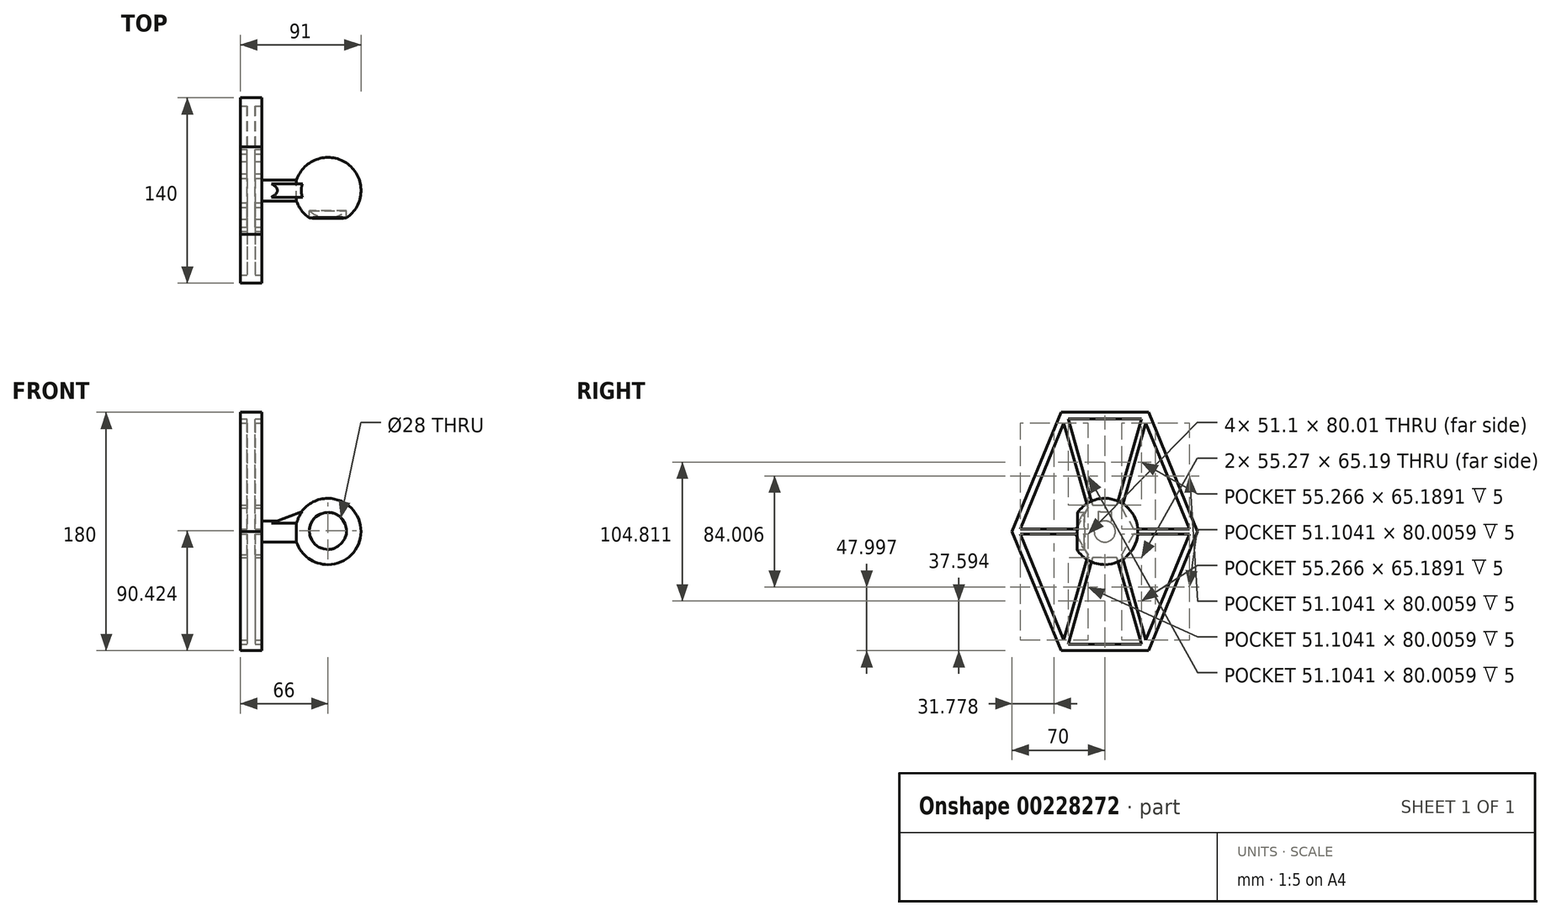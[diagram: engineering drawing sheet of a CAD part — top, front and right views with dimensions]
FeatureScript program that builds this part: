
annotation { "Feature Type Name" : "Feature", "Feature Type Description" : "" }
export const myFeature = defineFeature(function(context is Context, id is Id, definition is map)
    precondition{}
    {
        {
            var Q0;
            Q0=qCreatedBy(makeId("Front.planeOp"),FACE);
            var sketch = newSketch(context, id + "F0", { "sketchPlane" : qUnion([Q0])});
            skArc(sketch, "E0", {"start": v(0, -25) * mm, "mid": v(25, 0) * mm, "end": v(0, 25) * mm});
            skLineSegment(sketch, "E1", {"start": v(0, 25) * mm, "end": v(0, -25) * mm});
            skSolve(sketch);
        }
        {
            var Q0;
            Q0=qSketchRegion(id+"F0",true);
            var Q1;
            Q1=sQuery(id+"F0.wireOp",EDGE,"E1");
            revolve(context, id + "F1", {"entities" : qUnion([Q0]), "axis" : qUnion([Q1]), "revolveType" : RevolveType.FULL});
        }
        {
            var Q0;
            Q0=qCreatedBy(makeId("Front.planeOp"),FACE);
            var sketch = newSketch(context, id + "F2", { "sketchPlane" : qUnion([Q0])});
            skLineSegment(sketch, "E2.bottom", {"start": v(0, 0) * mm, "end": v(-55, 0) * mm});
            skLineSegment(sketch, "E2.top", {"start": v(0, 8) * mm, "end": v(-55, 8) * mm});
            skLineSegment(sketch, "E2.left", {"start": v(0, 0) * mm, "end": v(0, 8) * mm});
            skLineSegment(sketch, "E2.right", {"start": v(-55, 0) * mm, "end": v(-55, 8) * mm});
            skSolve(sketch);
        }
        {
            var Q0;
            Q0=qSketchRegion(id+"F2",true);
            var Q1;
            Q1=sQuery(id+"F2.wireOp",EDGE,"E2.bottom");
            revolve(context, id + "F3", {"operationType" : NewBodyOperationType.ADD, "entities" : qUnion([Q0]), "axis" : qUnion([Q1]), "revolveType" : RevolveType.FULL});
        }
        {
            var Q0;
            Q0=makeQuery(id+"F3.opRevolve","SWEPT_FACE",FACE,{"disambiguationData":[OSD([sQuery(id+"F2.wireOp",EDGE,"E2.right")])]});
            var sketch = newSketch(context, id + "F4", { "sketchPlane" : qUnion([Q0])});
            skLineSegment(sketch, "E3", {"start": v(0, 90) * mm, "end": v(-33.06, 90) * mm});
            skLineSegment(sketch, "E4", {"start": v(-33.06, 90) * mm, "end": v(-70, 0) * mm});
            skLineSegment(sketch, "E5", {"start": v(-70, 0) * mm, "end": v(0, 0) * mm, "construction": true});
            skLineSegment(sketch, "E6", {"start": v(0, 0) * mm, "end": v(0, 90) * mm, "construction": true});
            skLineSegment(sketch, "E7.MirrorCS", {"start": v(-33.06, -90) * mm, "end": v(-70, 0) * mm});
            skLineSegment(sketch, "E8.MirrorCS", {"start": v(0, -90) * mm, "end": v(-33.06, -90) * mm});
            skLineSegment(sketch, "E9.MirrorCS", {"start": v(0, 90) * mm, "end": v(33.06, 90) * mm});
            skLineSegment(sketch, "E10.MirrorCS", {"start": v(33.06, 90) * mm, "end": v(70, 0) * mm});
            skLineSegment(sketch, "E11.MirrorCS", {"start": v(33.06, -90) * mm, "end": v(70, 0) * mm});
            skLineSegment(sketch, "E12.MirrorCS", {"start": v(0, -90) * mm, "end": v(33.06, -90) * mm});
            skSolve(sketch);
        }
        {
            var Q0;
            Q0=qSketchRegion(id+"F4",true);
            extrude(context, id + "F5", {"entities" : qUnion([Q0]), "operationType" : NewBodyOperationType.ADD, "depth" : 6 * mm});
        }
        {
            var Q0;
            Q0=makeQuery(id+"F5.opExtrude","CAP_FACE",FACE,{"disambiguationData":[OSD([sQuery(id+"F4.wireOp",EDGE,"E3"),sQuery(id+"F4.wireOp",EDGE,"E4"),sQuery(id+"F4.wireOp",EDGE,"E7.MirrorCS"),sQuery(id+"F4.wireOp",EDGE,"E8.MirrorCS"),sQuery(id+"F4.wireOp",EDGE,"E9.MirrorCS"),sQuery(id+"F4.wireOp",EDGE,"E10.MirrorCS"),sQuery(id+"F4.wireOp",EDGE,"E11.MirrorCS"),sQuery(id+"F4.wireOp",EDGE,"E12.MirrorCS")])],"isStart":false});
            var sketch = newSketch(context, id + "F6", { "sketchPlane" : qUnion([Q0])});
            skLineSegment(sketch, "E13.0", {"start": v(-30.94, 82) * mm, "end": v(-12.67, 17.68) * mm});
            skLineSegment(sketch, "E14.0", {"start": v(-27.63, 85) * mm, "end": v(-9.12, 19.81) * mm});
            skLineSegment(sketch, "E15.0", {"start": v(-63.77, -2) * mm, "end": v(-21.72, -2) * mm});
            skLineSegment(sketch, "E16.0", {"start": v(-63.77, 2) * mm, "end": v(-21.72, 2) * mm});
            skLineSegment(sketch, "E17", {"start": v(0, 0) * mm, "end": v(0, -57.76) * mm, "construction": true});
            skLineSegment(sketch, "E18", {"start": v(0, 0) * mm, "end": v(92.77, 0) * mm, "construction": true});
            skLineSegment(sketch, "E19.MirrorCS", {"start": v(63.77, -2) * mm, "end": v(21.72, -2) * mm});
            skLineSegment(sketch, "E20.MirrorCS", {"start": v(63.77, 2) * mm, "end": v(21.72, 2) * mm});
            skLineSegment(sketch, "E21.MirrorCS", {"start": v(30.94, 82) * mm, "end": v(12.67, 17.68) * mm});
            skLineSegment(sketch, "E22.MirrorCS", {"start": v(27.63, 85) * mm, "end": v(9.12, 19.81) * mm});
            skLineSegment(sketch, "E23.MirrorCS", {"start": v(-30.94, -82) * mm, "end": v(-12.67, -17.68) * mm});
            skLineSegment(sketch, "E24.MirrorCS", {"start": v(-27.63, -85) * mm, "end": v(-9.12, -19.81) * mm});
            skLineSegment(sketch, "E25.MirrorCS", {"start": v(27.63, -85) * mm, "end": v(9.12, -19.81) * mm});
            skLineSegment(sketch, "E26.MirrorCS", {"start": v(30.94, -82) * mm, "end": v(12.67, -17.68) * mm});
            skLineSegment(sketch, "E27.0", {"start": v(-9.12, 19.81) * mm, "end": v(9.12, 19.81) * mm});
            skLineSegment(sketch, "E27.1", {"start": v(12.67, 17.68) * mm, "end": v(21.72, 2) * mm});
            skLineSegment(sketch, "E27.2", {"start": v(21.72, -2) * mm, "end": v(12.67, -17.68) * mm});
            skLineSegment(sketch, "E27.3", {"start": v(9.12, -19.81) * mm, "end": v(-9.12, -19.81) * mm});
            skLineSegment(sketch, "E27.4", {"start": v(-12.67, -17.68) * mm, "end": v(-21.72, -2) * mm});
            skLineSegment(sketch, "E27.5", {"start": v(-21.72, 2) * mm, "end": v(-12.67, 17.68) * mm});
            skPoint(sketch, "E27.0.midPoint", {"position": v(0, 19.81) * mm});
            skPoint(sketch, "E28.end.orphan", {"position": v(-10.36, 9.54) * mm});
            skPoint(sketch, "E28.start.orphan", {"position": v(-6.97, 12.24) * mm});
            skPoint(sketch, "E29.orphan", {"position": v(-11.44, 19.81) * mm});
            skPoint(sketch, "E30.end.orphan", {"position": v(6.97, 12.24) * mm});
            skPoint(sketch, "E30.start.orphan", {"position": v(10.36, 9.54) * mm});
            skPoint(sketch, "E31.orphan", {"position": v(11.44, 19.81) * mm});
            skPoint(sketch, "E32.orphan", {"position": v(14.09, 2) * mm});
            skPoint(sketch, "E33.MirrorCS.end.orphan", {"position": v(14.09, -2) * mm});
            skPoint(sketch, "E34.end.orphan", {"position": v(10.36, -9.54) * mm});
            skPoint(sketch, "E35.orphan", {"position": v(6.97, -12.24) * mm});
            skPoint(sketch, "E36.end.orphan", {"position": v(-6.97, -12.24) * mm});
            skPoint(sketch, "E36.start.orphan", {"position": v(-10.36, -9.54) * mm});
            skPoint(sketch, "E37.end.orphan", {"position": v(-14.09, -2) * mm});
            skPoint(sketch, "E37.start.orphan", {"position": v(-14.09, 2) * mm});
            skLineSegment(sketch, "E38.0", {"start": v(-33.06, 90) * mm, "end": v(-70, 0) * mm});
            skLineSegment(sketch, "E38.1", {"start": v(-33.06, -90) * mm, "end": v(33.06, -90) * mm});
            skLineSegment(sketch, "E38.2", {"start": v(33.06, -90) * mm, "end": v(70, 0) * mm});
            skLineSegment(sketch, "E38.3", {"start": v(-70, 0) * mm, "end": v(-33.06, -90) * mm});
            skLineSegment(sketch, "E38.4", {"start": v(70, 0) * mm, "end": v(33.06, 90) * mm});
            skLineSegment(sketch, "E38.5", {"start": v(33.06, 90) * mm, "end": v(-33.06, 90) * mm});
            skLineSegment(sketch, "E39.0", {"start": v(27.63, 85) * mm, "end": v(-27.63, 85) * mm});
            skLineSegment(sketch, "E39.1", {"start": v(-63.77, -2) * mm, "end": v(-30.94, -82) * mm});
            skLineSegment(sketch, "E39.2", {"start": v(-27.63, -85) * mm, "end": v(27.63, -85) * mm});
            skLineSegment(sketch, "E39.3", {"start": v(-30.94, 82) * mm, "end": v(-63.77, 2) * mm});
            skLineSegment(sketch, "E39.4", {"start": v(30.94, -82) * mm, "end": v(63.77, -2) * mm});
            skLineSegment(sketch, "E39.5", {"start": v(63.77, 2) * mm, "end": v(30.94, 82) * mm});
            skPoint(sketch, "E40.orphan", {"position": v(-31.64, 84.45) * mm});
            skPoint(sketch, "E41.orphan", {"position": v(-27.79, 85.55) * mm});
            skPoint(sketch, "E42.orphan", {"position": v(31.64, 84.45) * mm});
            skPoint(sketch, "E43.orphan", {"position": v(27.79, 85.55) * mm});
            skPoint(sketch, "E44.orphan", {"position": v(64.6, 2) * mm});
            skPoint(sketch, "E45.MirrorCS.end.orphan", {"position": v(64.6, -2) * mm});
            skPoint(sketch, "E46.orphan", {"position": v(31.64, -84.45) * mm});
            skPoint(sketch, "E47.orphan", {"position": v(27.79, -85.55) * mm});
            skPoint(sketch, "E48.orphan", {"position": v(-31.64, -84.45) * mm});
            skPoint(sketch, "E49.orphan", {"position": v(-27.79, -85.55) * mm});
            skPoint(sketch, "E50.orphan", {"position": v(-64.6, 2) * mm});
            skPoint(sketch, "E51.orphan", {"position": v(-64.6, -2) * mm});
            skSolve(sketch);
        }
        {
            var Q0;
            Q0=makeQuery(id+"F6.imprint","IMPRINT",FACE,{"disambiguationData":[TD([[makeQuery(id+"F6.imprint","IMPRINT",EDGE,{"derivedFrom":sQuery(id+"F6.wireOp",EDGE,"E13.0")}),1.0]])]});
            extrude(context, id + "F7", {"entities" : qUnion([Q0]), "operationType" : NewBodyOperationType.ADD, "depth" : 5 * mm, "hasSecondDirection" : true, "secondDirectionOppositeDirection" : true, "secondDirectionDepth" : 11 * mm});
        }
        {
            var Q0;
            Q0=qCreatedBy(makeId("Front.planeOp"),FACE);
            var sketch = newSketch(context, id + "F8", { "sketchPlane" : qUnion([Q0])});
            skLineSegment(sketch, "E52", {"start": v(-42.94, 6.13) * mm, "end": v(-15.73, 6.13) * mm});
            skLineSegment(sketch, "E53", {"start": v(-15.73, 6.13) * mm, "end": v(-15.73, 16.54) * mm});
            skLineSegment(sketch, "E54", {"start": v(-15.73, 16.54) * mm, "end": v(-42.94, 6.13) * mm});
            skSolve(sketch);
        }
        {
            var Q0;
            Q0=makeQuery(id+"F8.imprint","IMPRINT",FACE,{"disambiguationData":[TD([[makeQuery(id+"F8.imprint","IMPRINT",EDGE,{"derivedFrom":sQuery(id+"F8.wireOp",EDGE,"E52")}),1.0]])]});
            extrude(context, id + "F9", {"entities" : qUnion([Q0]), "operationType" : NewBodyOperationType.ADD, "depth" : 5 * mm, "hasSecondDirection" : true, "secondDirectionOppositeDirection" : true, "secondDirectionDepth" : 5 * mm});
        }
        {
            var Q0;
            Q0=qCreatedBy(makeId("Front.planeOp"),FACE);
            var sketch = newSketch(context, id + "F10", { "sketchPlane" : qUnion([Q0])});
            skCircle(sketch, "E55", {"center": v(0, 0.42) * mm, "radius": 14 * mm});
            skSolve(sketch);
        }
        {
            var Q0;
            Q0 = qSketchRegion(id + "F10", true);
            extrude(context, id + "F11", {"entities" : qUnion([Q0]), "operationType" : NewBodyOperationType.REMOVE, "depth" : 25 * mm});
        }
        {
            var Q0;
            Q0=qCreatedBy(makeId("Front.planeOp"),FACE);
            var sketch = newSketch(context, id + "F12", { "sketchPlane" : qUnion([Q0])});
            skArc(sketch, "E56", {"start": v(0, -20.57) * mm, "mid": v(20.72, 0.42) * mm, "end": v(0, 21.42) * mm});
            skLineSegment(sketch, "E57", {"start": v(0, 21.42) * mm, "end": v(0, -20.57) * mm});
            skSolve(sketch);
        }
        {
            var Q0;
            Q0=makeQuery(id+"F12.imprint","IMPRINT",FACE,{"disambiguationData":[TD([[makeQuery(id+"F12.imprint","IMPRINT",EDGE,{"derivedFrom":sQuery(id+"F12.wireOp",EDGE,"E56")}),1.0]])]});
            var Q1;
            Q1=sQuery(id+"F12.wireOp",EDGE,"E57");
            revolve(context, id + "F13", {"operationType" : NewBodyOperationType.ADD, "entities" : qUnion([Q0]), "axis" : qUnion([Q1]), "revolveType" : RevolveType.FULL});
        }
    });
